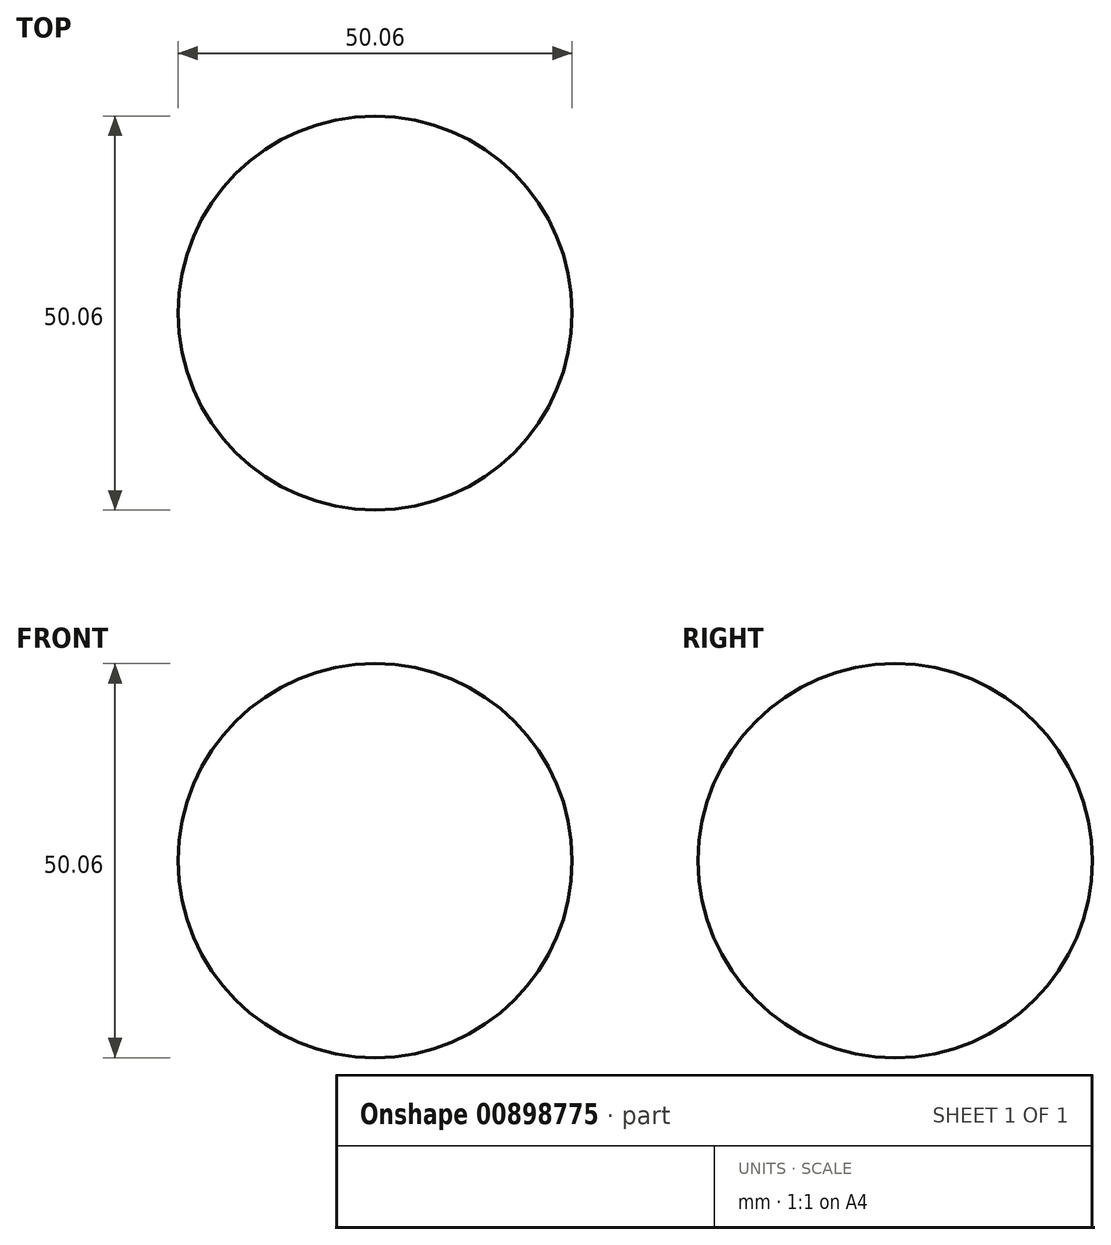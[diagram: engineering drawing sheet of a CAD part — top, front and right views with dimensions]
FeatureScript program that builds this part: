
annotation { "Feature Type Name" : "Feature", "Feature Type Description" : "" }
export const myFeature = defineFeature(function(context is Context, id is Id, definition is map)
    precondition{}
    {
        {
            var Q0;
            Q0=qCreatedBy(makeId("Front.planeOp"),FACE);
            var sketch = newSketch(context, id + "F0", { "sketchPlane" : qUnion([Q0])});
            skArc(sketch, "E0", {"start": v(0, 25.03) * mm, "mid": v(-25.03, 0) * mm, "end": v(0, -25.03) * mm});
            skLineSegment(sketch, "E1", {"start": v(0, 25.03) * mm, "end": v(0, -25.03) * mm});
            skSolve(sketch);
        }
        {
            var Q0;
            Q0=makeQuery(id+"F0.imprint","IMPRINT",FACE,{"disambiguationData":[TD([[makeQuery(id+"F0.imprint","IMPRINT",EDGE,{"derivedFrom":sQuery(id+"F0.wireOp",EDGE,"E0")}),1.0]])]});
            var Q1;
            Q1=sQuery(id+"F0.wireOp",EDGE,"E1");
            revolve(context, id + "F1", {"surfaceOperationType" : NewSurfaceOperationType.NEW, "entities" : qUnion([Q0]), "axis" : qUnion([Q1]), "revolveType" : RevolveType.FULL});
        }
    });
